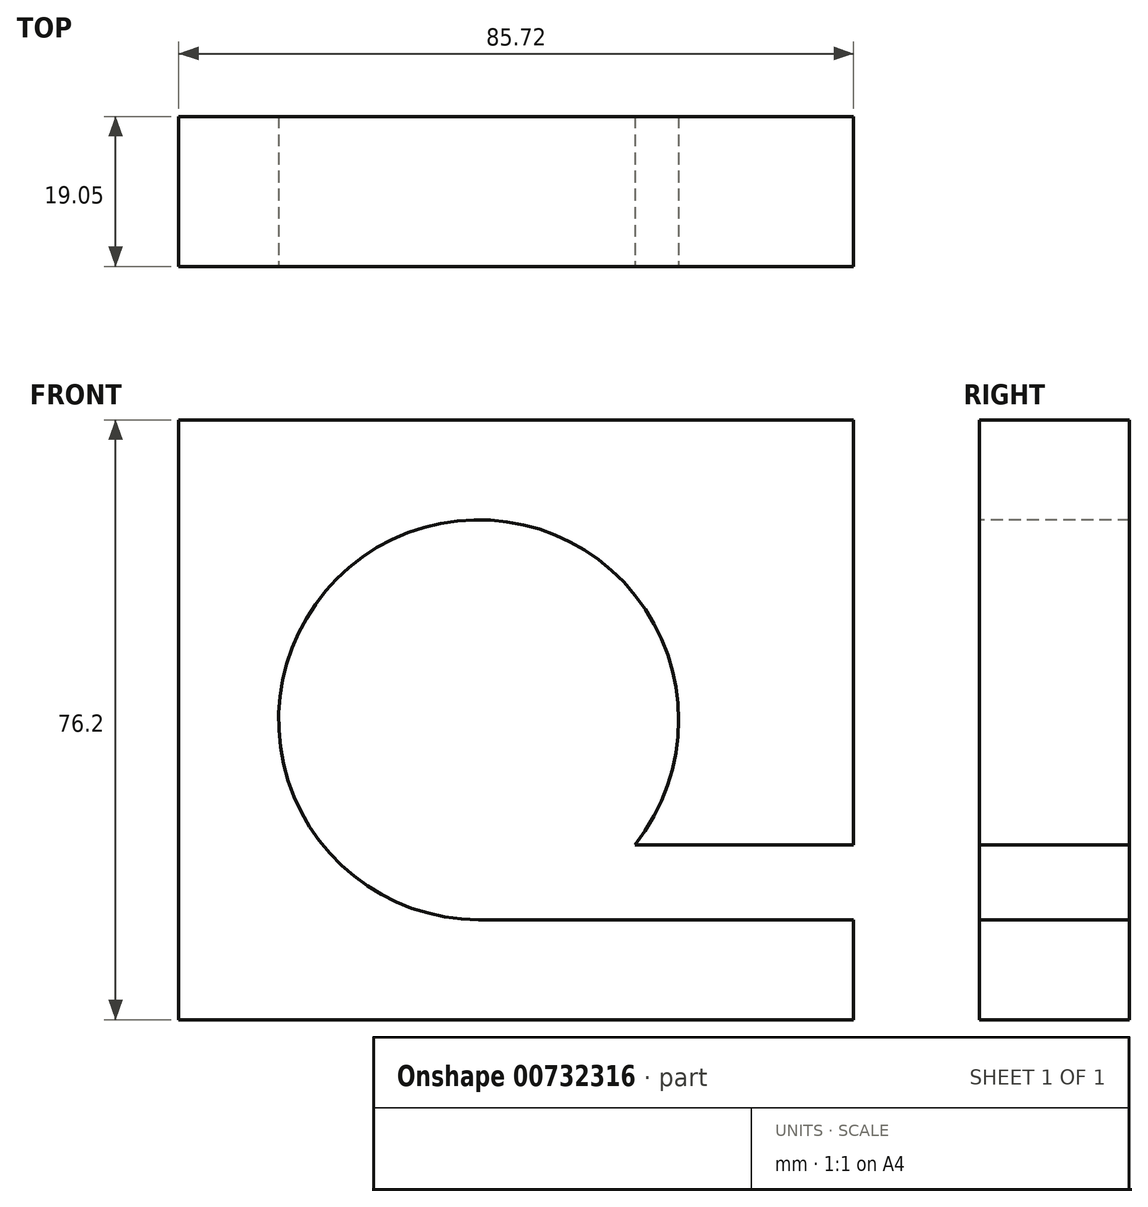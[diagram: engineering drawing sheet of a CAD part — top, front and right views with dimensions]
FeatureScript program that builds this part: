
annotation { "Feature Type Name" : "Feature", "Feature Type Description" : "" }
export const myFeature = defineFeature(function(context is Context, id is Id, definition is map)
    precondition{}
    {
        {
            var Q0;
            Q0=qCreatedBy(makeId("Front.planeOp"),FACE);
            var sketch = newSketch(context, id + "F0", { "sketchPlane" : qUnion([Q0])});
            skLineSegment(sketch, "E0.bottom", {"start": v(0, 0) * mm, "end": v(85.73, 0) * mm});
            skLineSegment(sketch, "E0.top", {"start": v(0, 76.2) * mm, "end": v(85.72, 76.2) * mm});
            skLineSegment(sketch, "E0.left", {"start": v(0, 0) * mm, "end": v(0, 76.2) * mm});
            skLineSegment(sketch, "E0.right", {"start": v(85.73, 0) * mm, "end": v(85.72, 76.2) * mm});
            skSolve(sketch);
        }
        {
            var Q0;
            Q0=makeQuery(id+"F0.imprint","IMPRINT",FACE,{"disambiguationData":[TD([[makeQuery(id+"F0.imprint","IMPRINT",EDGE,{"derivedFrom":sQuery(id+"F0.wireOp",EDGE,"E0.bottom")}),1.0]])]});
            extrude(context, id + "F1", {"entities" : qUnion([Q0]), "depth" : 19.05 * mm, "offsetDistance" : 25.4 * mm});
        }
        {
            var Q0;
            Q0=makeQuery(id+"F1.opExtrude","CAP_FACE",FACE,{"disambiguationData":[OSD([sQuery(id+"F0.wireOp",EDGE,"E0.bottom"),sQuery(id+"F0.wireOp",EDGE,"E0.top"),sQuery(id+"F0.wireOp",EDGE,"E0.left"),sQuery(id+"F0.wireOp",EDGE,"E0.right")])],"isStart":false});
            var sketch = newSketch(context, id + "F2", { "sketchPlane" : qUnion([Q0])});
            skCircle(sketch, "E1", {"center": v(38.1, 38.1) * mm, "radius": 25.4 * mm});
            skSolve(sketch);
        }
        {
            var Q0;
            Q0 = qSketchRegion(id + "F2", true);
            extrude(context, id + "F3", {"entities" : qUnion([Q0]), "operationType" : NewBodyOperationType.REMOVE, "oppositeDirection" : true, "depth" : 25.4 * mm, "offsetDistance" : 25.4 * mm});
        }
        {
            var Q0;
            Q0=makeQuery(id+"F1.opExtrude","CAP_FACE",FACE,{"disambiguationData":[OSD([sQuery(id+"F0.wireOp",EDGE,"E0.bottom"),sQuery(id+"F0.wireOp",EDGE,"E0.top"),sQuery(id+"F0.wireOp",EDGE,"E0.left"),sQuery(id+"F0.wireOp",EDGE,"E0.right")])],"isStart":false});
            var sketch = newSketch(context, id + "F4", { "sketchPlane" : qUnion([Q0])});
            skLineSegment(sketch, "E2", {"start": v(85.73, 22.23) * mm, "end": v(57.93, 22.23) * mm});
            skLineSegment(sketch, "E3", {"start": v(57.93, 22.23) * mm, "end": v(38.1, 12.7) * mm});
            skLineSegment(sketch, "E4", {"start": v(38.1, 12.7) * mm, "end": v(85.73, 12.7) * mm});
            skLineSegment(sketch, "E5", {"start": v(85.72, 12.7) * mm, "end": v(85.72, 22.23) * mm});
            skSolve(sketch);
        }
        {
            var Q0;
            Q0 = qSketchRegion(id + "F4", true);
            extrude(context, id + "F5", {"entities" : qUnion([Q0]), "operationType" : NewBodyOperationType.REMOVE, "oppositeDirection" : true, "depth" : 25.4 * mm, "offsetDistance" : 25.4 * mm});
        }
    });
